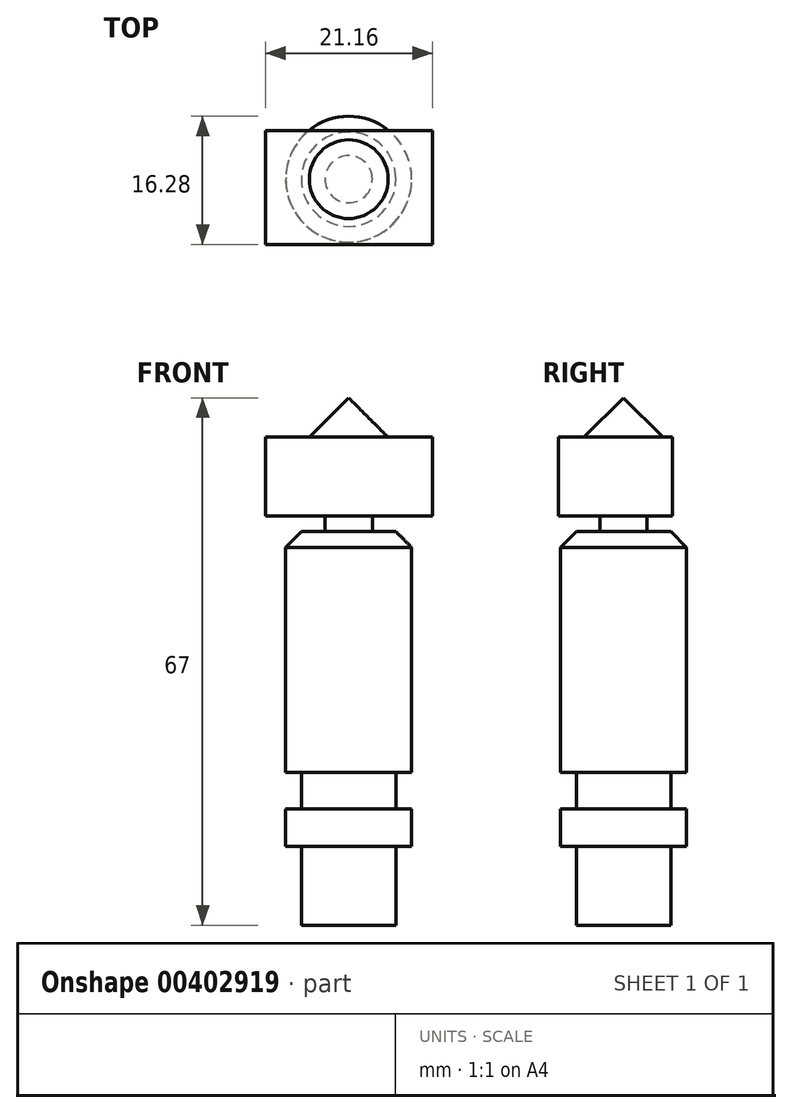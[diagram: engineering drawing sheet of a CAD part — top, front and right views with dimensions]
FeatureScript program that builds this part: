
annotation { "Feature Type Name" : "Feature", "Feature Type Description" : "" }
export const myFeature = defineFeature(function(context is Context, id is Id, definition is map)
    precondition{}
    {
        {
            var Q0;
            Q0=qCreatedBy(makeId("Top.planeOp"),FACE);
            var sketch = newSketch(context, id + "F0", { "sketchPlane" : qUnion([Q0])});
            skCircle(sketch, "E0", {"center": v(0, 0) * mm, "radius": 8 * mm});
            skSolve(sketch);
        }
        {
            var Q0;
            Q0 = qSketchRegion(id + "F0", true);
            extrude(context, id + "F1", {"entities" : qUnion([Q0]), "depth" : 4.8 * mm, "offsetDistance" : 25 * mm});
        }
        {
            var Q0;
            Q0=makeQuery(id+"F1.opExtrude","CAP_FACE",FACE,{"disambiguationData":[OSD([sQuery(id+"F0.wireOp",EDGE,"E0")])],"isStart":false});
            var sketch = newSketch(context, id + "F2", { "sketchPlane" : qUnion([Q0])});
            skCircle(sketch, "E1", {"center": v(0, 0) * mm, "radius": 6 * mm});
            skSolve(sketch);
        }
        {
            var Q0;
            Q0 = qSketchRegion(id + "F2", true);
            extrude(context, id + "F3", {"entities" : qUnion([Q0]), "operationType" : NewBodyOperationType.ADD, "depth" : 4.6 * mm, "offsetDistance" : 25 * mm});
        }
        {
            var Q0;
            Q0=makeQuery(id+"F3.opExtrude","CAP_FACE",FACE,{"disambiguationData":[OSD([sQuery(id+"F2.wireOp",EDGE,"E1")])],"isStart":false});
            var sketch = newSketch(context, id + "F4", { "sketchPlane" : qUnion([Q0])});
            skCircle(sketch, "E2", {"center": v(0, 0) * mm, "radius": 8 * mm});
            skSolve(sketch);
        }
        {
            var Q0;
            Q0 = qSketchRegion(id + "F4", true);
            extrude(context, id + "F5", {"entities" : qUnion([Q0]), "operationType" : NewBodyOperationType.ADD, "depth" : 30.6 * mm, "offsetDistance" : 25 * mm});
        }
        {
            var Q0;
            Q0=makeQuery(id+"F5.opExtrude","CAP_EDGE",EDGE,{"disambiguationData":[OSD([sQuery(id+"F4.wireOp",EDGE,"E2")])],"isStart":false});
            chamfer(context, id + "F6", {"entities" : qUnion([Q0]), "width" : 2 * mm, "tangentPropagation" : true});
        }
        {
            var Q0;
            Q0=makeQuery(id+"F5.opExtrude","CAP_FACE",FACE,{"disambiguationData":[OSD([sQuery(id+"F4.wireOp",EDGE,"E2")])],"isStart":false});
            var sketch = newSketch(context, id + "F7", { "sketchPlane" : qUnion([Q0])});
            skCircle(sketch, "E3", {"center": v(0, 0) * mm, "radius": 3 * mm});
            skSolve(sketch);
        }
        {
            var Q0;
            Q0 = qSketchRegion(id + "F7", true);
            extrude(context, id + "F8", {"entities" : qUnion([Q0]), "operationType" : NewBodyOperationType.ADD, "depth" : 2 * mm, "offsetDistance" : 25 * mm});
        }
        {
            var Q0;
            Q0=makeQuery(id+"F8.opExtrude","CAP_FACE",FACE,{"disambiguationData":[OSD([sQuery(id+"F7.wireOp",EDGE,"E3")])],"isStart":false});
            var sketch = newSketch(context, id + "F9", { "sketchPlane" : qUnion([Q0])});
            skLineSegment(sketch, "E4.bottom", {"start": v(-10.54, 6.2) * mm, "end": v(10.62, 6.2) * mm});
            skLineSegment(sketch, "E4.top", {"start": v(-10.54, -8.28) * mm, "end": v(10.62, -8.28) * mm});
            skLineSegment(sketch, "E4.left", {"start": v(-10.54, 6.2) * mm, "end": v(-10.54, -8.28) * mm});
            skLineSegment(sketch, "E4.right", {"start": v(10.62, 6.2) * mm, "end": v(10.62, -8.28) * mm});
            skSolve(sketch);
        }
        {
            var Q0;
            Q0 = qSketchRegion(id + "F9", true);
            extrude(context, id + "F10", {"entities" : qUnion([Q0]), "operationType" : NewBodyOperationType.ADD, "depth" : 10 * mm, "offsetDistance" : 25 * mm});
        }
        {
            var Q0;
            Q0=makeQuery(id+"F10.opExtrude","CAP_FACE",FACE,{"disambiguationData":[OSD([sQuery(id+"F9.wireOp",EDGE,"E4.bottom"),sQuery(id+"F9.wireOp",EDGE,"E4.top"),sQuery(id+"F9.wireOp",EDGE,"E4.left"),sQuery(id+"F9.wireOp",EDGE,"E4.right")])],"isStart":false});
            var sketch = newSketch(context, id + "F11", { "sketchPlane" : qUnion([Q0])});
            skCircle(sketch, "E5", {"center": v(0, 0) * mm, "radius": 5 * mm});
            skSolve(sketch);
        }
        {
            var Q0;
            Q0 = qSketchRegion(id + "F11", true);
            extrude(context, id + "F12", {"entities" : qUnion([Q0]), "operationType" : NewBodyOperationType.ADD, "depth" : 5 * mm, "offsetDistance" : 25 * mm, "hasDraft" : true, "draftAngle" : 45 * degree, "draftPullDirection" : true});
        }
        {
            var Q0;
            Q0=makeQuery(id+"F1.opExtrude","CAP_FACE",FACE,{"disambiguationData":[OSD([sQuery(id+"F0.wireOp",EDGE,"E0")])],"isStart":true});
            var sketch = newSketch(context, id + "F13", { "sketchPlane" : qUnion([Q0])});
            skCircle(sketch, "E6", {"center": v(0, 0) * mm, "radius": 6 * mm});
            skSolve(sketch);
        }
        {
            var Q0;
            Q0 = qSketchRegion(id + "F13", true);
            extrude(context, id + "F14", {"entities" : qUnion([Q0]), "operationType" : NewBodyOperationType.ADD, "depth" : 10 * mm, "offsetDistance" : 25 * mm});
        }
    });
